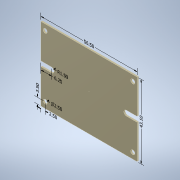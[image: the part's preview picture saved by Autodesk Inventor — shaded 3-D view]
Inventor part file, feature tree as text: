
AUTODESK INVENTOR PART (.ipt)
format: ipt  version: 2022 (Build 260153000, 153)  size: 175,104 bytes
history: native  units: in
note: dims shown in document units (in); Inventor stores cm internally (conversion verified against a paired STEP export)
features: other x8, extrude x1, sketch x1
ambient origin geometry x8: Origin, YZ Plane, XZ Plane, XY Plane, X Axis, Y Axis, Z Axis, Center Point
bodies: Solid2 (feature_tree), Solid1 (feature_tree)
feature tree (10):
  other  "Annotations"
  extrude  "Extrusion1"  Depth=0.7894in
  sketch  "Sketch1"  dims[d0=0.1181in d1=0.7894in d2=0.7894in d4=0.2461in d5=0.0in d6=0.0in d13=0.0in d14=0.3937in d15=0.2461in d16=1.6969in d20=1.2189in d21=0.0591in d22=0.3743in d23=0.1378in d24=0.0961in d25=0.0984in d26=1.4765in d27=0.0984in d7=0.0in d8=0.3937in d9=2.2244in]
  other  "Linear Dimension 1"
  other  "Linear Dimension 3"
  other  "Linear Dimension 4"
  other  "Radial Dimension 1"
  other  "Linear Dimension 5"
  other  "Linear Dimension 6"
  other  "Diameter Dimension 2"
